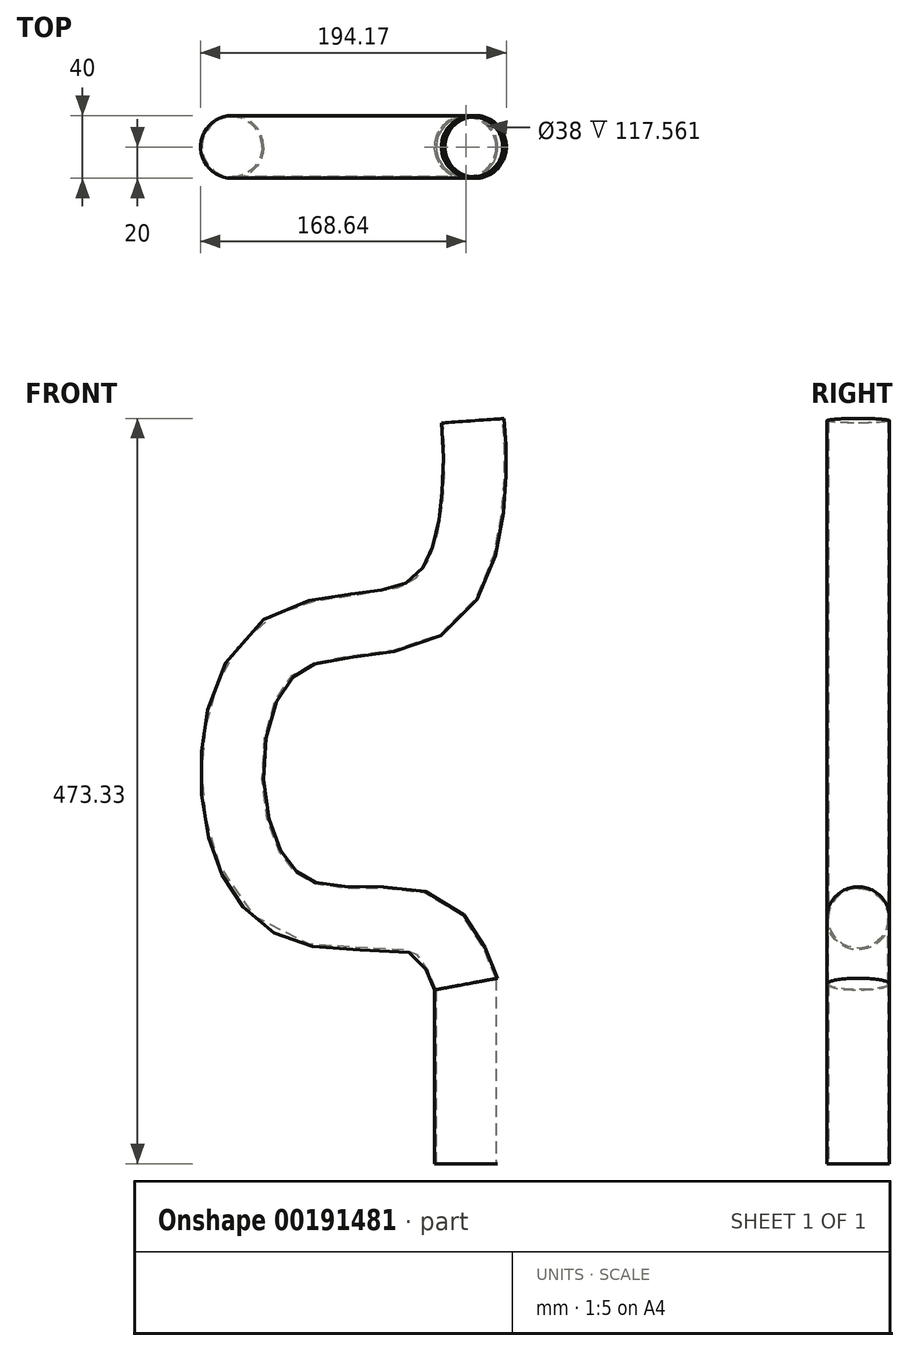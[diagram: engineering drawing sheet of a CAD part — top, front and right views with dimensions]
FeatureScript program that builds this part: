
annotation { "Feature Type Name" : "Feature", "Feature Type Description" : "" }
export const myFeature = defineFeature(function(context is Context, id is Id, definition is map)
    precondition{}
    {
        {
            var Q0;
            Q0=qCreatedBy(makeId("Top.planeOp"),FACE);
            var sketch = newSketch(context, id + "F0", { "sketchPlane" : qUnion([Q0])});
            skCircle(sketch, "E0", {"center": v(0, 0) * mm, "radius": 19 * mm});
            skCircle(sketch, "E1", {"center": v(0, 0) * mm, "radius": 20 * mm});
            skSolve(sketch);
        }
        {
            var Q0;
            Q0 = qSketchRegion(id + "F0", true);
            extrude(context, id + "F1", {"entities" : qUnion([Q0]), "depth" : 10 * mm});
        }
        {
            var Q0;
            Q0=qCreatedBy(makeId("Front.planeOp"),FACE);
            var sketch = newSketch(context, id + "F2", { "sketchPlane" : qUnion([Q0])});
            skLineSegment(sketch, "E2", {"start": v(0, 0) * mm, "end": v(0, 114.07) * mm});
            skFitSpline(sketch, "E3", {"points": [v(0, 114.07) * mm, v(-26.97, 152.13) * mm, v(-103.64, 160.08) * mm, v(-147.38, 228.8) * mm, v(-116.14, 329.9) * mm, v(-24.13, 353.75) * mm, v(4.84, 425.88) * mm, v(4.27, 471.88) * mm], "startDerivative": vector(-160.71, 422.95) * mm, "endDerivative": vector(-26.16, 361.38) * mm});
            skSolve(sketch);
        }
        {
            var Q0;
            Q0=makeQuery(id+"F1.opExtrude","CAP_FACE",FACE,{"disambiguationData":[OSD([sQuery(id+"F0.wireOp",EDGE,"E0"),sQuery(id+"F0.wireOp",EDGE,"E1")])],"isStart":false});
            var Q1;
            Q1=makeQuery(id+"F1.opExtrude","CAP_EDGE",EDGE,{"disambiguationData":[OSD([sQuery(id+"F0.wireOp",EDGE,"E0")])],"isStart":false});
            var Q2;
            Q2=sQuery(id+"F2.wireOp",EDGE,"E2");
            var Q3;
            Q3=sQuery(id+"F2.wireOp",EDGE,"E3");
            sweep(context, id + "F3", {"operationType" : NewBodyOperationType.ADD, "profiles" : qUnion([Q0]), "surfaceProfiles" : qUnion([Q1]), "path" : qUnion([Q2, Q3])});
        }
    });
